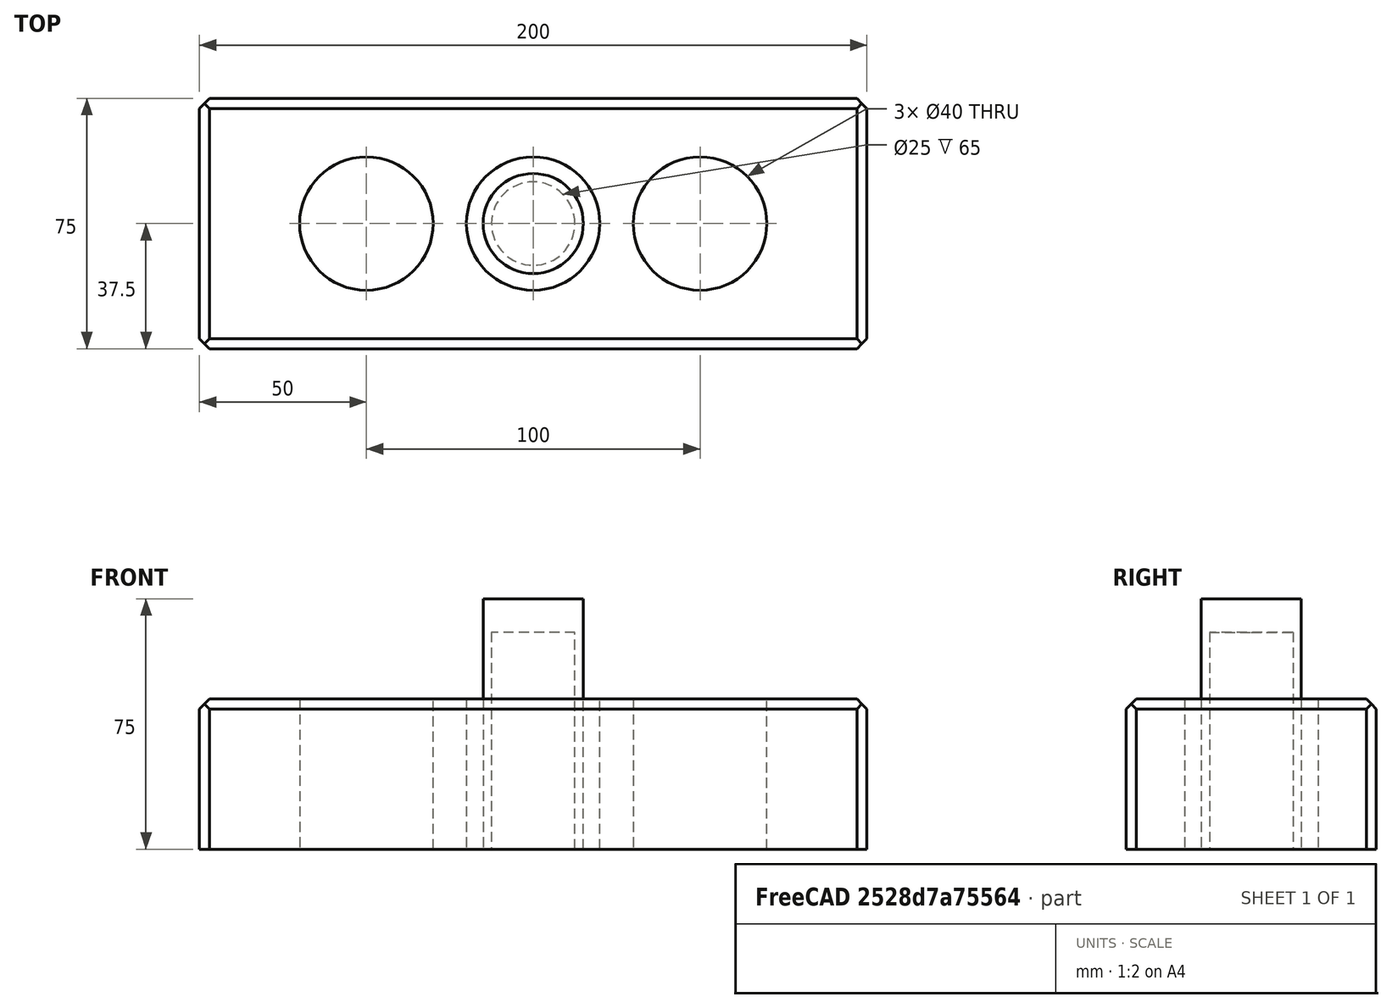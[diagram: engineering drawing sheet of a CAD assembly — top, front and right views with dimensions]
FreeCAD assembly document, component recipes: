
FREECAD ASSEMBLY — COMPONENT RECIPES ("AssemblyFile")

This assembly document has 2 components, labeled P0..P1 below (a component is one placed body or linked part). 2 of them carry a construction recipe — the FreeCAD feature program that regenerates the part from scratch, quoted from this document or its linked companion documents; the rest are supplied as boundary geometry only. No exploded tour is included for this assembly.
COMPONENT P0 — recipe-attached ("MainBody", modeled in this document).
Construction recipe (the document's own serialized feature program — sketch geometry with constraints, then the solid features built on it; lengths are millimeters unless a unit is written):

FEATURE [Sketcher::SketchObject] Sketch001
  FullyConstrained = true
  MapMode = 5
  Support = -> [XY_Plane002]
  expr: Constraints[17] = 40 / 2
  sketch-geometry (7):
    g0: LineSegment StartX=-100 StartY=37.5 StartZ=0 EndX=100 EndY=37.5 EndZ=0
    g1: LineSegment StartX=100 StartY=37.5 StartZ=0 EndX=100 EndY=-37.5 EndZ=0
    g2: LineSegment StartX=100 StartY=-37.5 StartZ=0 EndX=-100 EndY=-37.5 EndZ=0
    g3: LineSegment StartX=-100 StartY=-37.5 StartZ=0 EndX=-100 EndY=37.5 EndZ=0
    g4: Circle CenterX=0 CenterY=0 CenterZ=0 NormalX=0 NormalY=0 NormalZ=1 AngleXU=0 Radius=20
    g5: Circle CenterX=-50 CenterY=0 CenterZ=0 NormalX=0 NormalY=0 NormalZ=1 AngleXU=0 Radius=20
    g6: Circle CenterX=50 CenterY=0 CenterZ=0 NormalX=0 NormalY=0 NormalZ=1 AngleXU=0 Radius=20
  constraints (18):
    c: Coincident(g0,g1)
    c: Coincident(g1,g2)
    c: Coincident(g2,g3)
    c: Coincident(g3,g0)
    c: Horizontal(g0)
    c: Horizontal(g2)
    c: Vertical(g1)
    c: Vertical(g3)
    c: Symmetric(g0,g1,g-1)
    c: Coincident(g4,g-1)
    c: PointOnObject(g5,g-1)
    c: DistanceX(g0,g0) = 200
    c: DistanceY(g3,g3) = 75
    c: Equal(g5,g4)
    c: Equal(g4,g6)
    c: Symmetric(g5,g6,g-2)
    c: DistanceX(g5,g4) = 50
    c: Radius(g5) = 20
FEATURE [PartDesign::Pad] Pad
  Direction = (1,1,1)
  Length = 45
  Length2 = 100
  Profile = -> Sketch001
  Type = 0
FEATURE [PartDesign::Chamfer] Chamfer
  Angle = 45
  Base = -> Pad [Edge7,Edge4,Edge12,Edge10]
  BaseFeature = -> Pad
  ChamferType = 0
  FlipDirection = false
  Size = 3
  Size2 = 1
  SupportTransform = false
FEATURE [PartDesign::Chamfer] Chamfer001
  Angle = 45
  Base = -> Chamfer [Edge4,Edge17,Edge5,Edge1]
  BaseFeature = -> Chamfer
  ChamferType = 0
  FlipDirection = false
  Size = 3
  Size2 = 1
  SupportTransform = false
FEATURE [PartDesign::CoordinateSystem] MainBodyLCS
  AttacherType = Attacher::AttachEngine3D
  AttachmentOffset = pos=(0,0,0) rot=(0,0,1;1.5708rad)
  MapMode = 11
  Placement = pos=(0,0,45) rot=(0,0,1;3.14159rad)
  Support = -> [Chamfer001]
FEATURE [PartDesign::Body] Body001  label="MainBody"
  Group = -> [Sketch001,Pad,Chamfer,Chamfer001,MainBodyLCS]
  Origin = -> Origin002
  Tip = -> Chamfer001
COMPONENT P1 — recipe-attached ("RodBody", modeled in this document).
Construction recipe (the document's own serialized feature program — sketch geometry with constraints, then the solid features built on it; lengths are millimeters unless a unit is written):

FEATURE [Sketcher::SketchObject] Sketch002  label="RodSketch"
  FullyConstrained = true
  MapMode = 5
  Support = -> [XY_Plane003]
  expr: Constraints[1] = 25 / 2
  sketch-geometry (1):
    g0: Circle CenterX=0 CenterY=0 CenterZ=0 NormalX=0 NormalY=0 NormalZ=1 AngleXU=0 Radius=12.5
  constraints (2):
    c: Coincident(g0,g-1)
    c: Radius(g0) = 12.5
FEATURE [Sketcher::SketchObject] Sketch003  label="RodSketch0"
  FullyConstrained = true
  MapMode = 5
  Support = -> [XY_Plane003]
  expr: Constraints[1] = 30 / 2
  sketch-geometry (1):
    g0: Circle CenterX=0 CenterY=0 CenterZ=0 NormalX=0 NormalY=0 NormalZ=1 AngleXU=0 Radius=15
  constraints (2):
    c: Coincident(g0,g-1)
    c: Radius(g0) = 15
FEATURE [PartDesign::Pad] Pad001  label="RodPad"
  Direction = (1,1,1)
  Length = 75
  Length2 = 100
  Profile = -> Sketch003
  Type = 0
FEATURE [PartDesign::Pocket] Pocket  label="RodPocket"
  BaseFeature = -> Pad001
  Length = 65
  Length2 = 100
  Profile = -> Sketch002
  Reversed = true
  Type = 0
FEATURE [PartDesign::CoordinateSystem] RodLCS
  AttacherType = Attacher::AttachEngine3D
  AttachmentOffset = pos=(0,0,0) rot=(0,0,1;1.5708rad)
  MapMode = 11
  Placement = pos=(0,0,75) rot=(0,0,1;3.14159rad)
  Support = -> [Pocket]
FEATURE [PartDesign::Body] Body002  label="RodBody"
  Group = -> [Sketch003,Pad001,Sketch002,Pocket,RodLCS]
  Origin = -> Origin003
  Tip = -> Pocket
PROVENANCE & LICENSES
A FreeCAD (.FCStd) document from a public repository crawl; recipes are the document's own serialized feature recipes (and, for linked parts, companion documents' recipes).
License: as declared in the source repository (recorded in the dataset sidecar).
